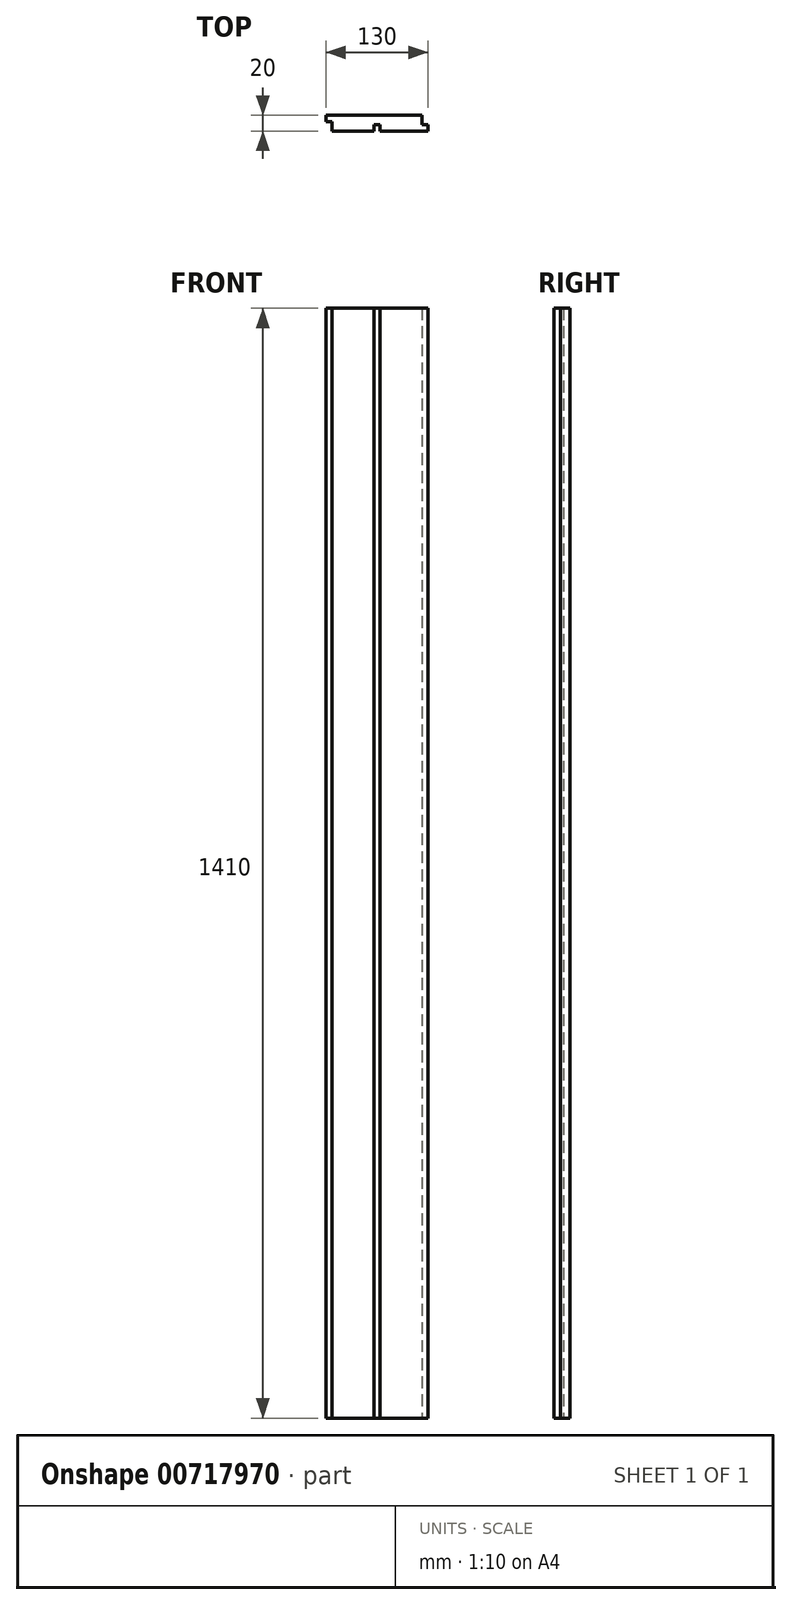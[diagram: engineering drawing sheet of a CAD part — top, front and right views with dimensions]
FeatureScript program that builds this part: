
annotation { "Feature Type Name" : "Feature", "Feature Type Description" : "" }
export const myFeature = defineFeature(function(context is Context, id is Id, definition is map)
    precondition{}
    {
        {
            var Q0;
            Q0=qCreatedBy(makeId("Front.planeOp"),FACE);
            var sketch = newSketch(context, id + "F0", { "sketchPlane" : qUnion([Q0])});
            skLineSegment(sketch, "E0.bottom", {"start": v(-374.72, 1144.48) * mm, "end": v(-244.72, 1144.48) * mm});
            skLineSegment(sketch, "E0.top", {"start": v(-374.72, -265.52) * mm, "end": v(-244.72, -265.52) * mm});
            skLineSegment(sketch, "E0.left", {"start": v(-374.72, 1144.48) * mm, "end": v(-374.72, -265.52) * mm});
            skLineSegment(sketch, "E0.right", {"start": v(-244.72, 1144.48) * mm, "end": v(-244.72, -265.52) * mm});
            skSolve(sketch);
        }
        {
            var Q0;
            Q0=makeQuery(id+"F0.imprint","IMPRINT",FACE,{"disambiguationData":[TD([[makeQuery(id+"F0.imprint","IMPRINT",EDGE,{"derivedFrom":sQuery(id+"F0.wireOp",EDGE,"E0.bottom")}),-1.0]])]});
            extrude(context, id + "F1", {"entities" : qUnion([Q0]), "oppositeDirection" : true, "depth" : 20 * mm, "offsetDistance" : 25.4 * mm});
        }
        {
            var Q0;
            Q0=makeQuery(id+"F1.opExtrude","CAP_FACE",FACE,{"disambiguationData":[OSD([sQuery(id+"F0.wireOp",EDGE,"E0.bottom"),sQuery(id+"F0.wireOp",EDGE,"E0.top"),sQuery(id+"F0.wireOp",EDGE,"E0.left"),sQuery(id+"F0.wireOp",EDGE,"E0.right")])],"isStart":true});
            var sketch = newSketch(context, id + "F2", { "sketchPlane" : qUnion([Q0])});
            skLineSegment(sketch, "E1.bottom", {"start": v(-313.72, 1144.48) * mm, "end": v(-305.72, 1144.48) * mm});
            skLineSegment(sketch, "E1.top", {"start": v(-313.72, -315.52) * mm, "end": v(-305.72, -315.52) * mm});
            skLineSegment(sketch, "E1.left", {"start": v(-313.72, 1144.48) * mm, "end": v(-313.72, -315.52) * mm});
            skLineSegment(sketch, "E1.right", {"start": v(-305.72, 1144.48) * mm, "end": v(-305.72, -315.52) * mm});
            skSolve(sketch);
        }
        {
            var Q0;
            Q0=makeQuery(id+"F2.imprint","IMPRINT",FACE,{"disambiguationData":[TD([[makeQuery(id+"F2.imprint","IMPRINT",EDGE,{"derivedFrom":sQuery(id+"F2.wireOp",EDGE,"E1.bottom")}),-1.0]])]});
            extrude(context, id + "F3", {"entities" : qUnion([Q0]), "operationType" : NewBodyOperationType.REMOVE, "oppositeDirection" : true, "depth" : 8 * mm, "offsetDistance" : 25.4 * mm});
        }
        {
            var Q0;
            {var subQ0=sQuery(id+"F0.wireOp",EDGE,"E0.bottom");var subQ1=sQuery(id+"F0.wireOp",EDGE,"E0.top");var subQ2=sQuery(id+"F0.wireOp",EDGE,"E0.left");Q0=makeQuery(id+"F3.boolean.opBoolean","SPLIT",FACE,{"disambiguationData":[TD([makeQuery(id+"F1.opExtrude","SWEPT_FACE",FACE,{"disambiguationData":[OSD([subQ2])]})])],"derivedFrom":makeQuery(id+"F1.opExtrude","CAP_FACE",FACE,{"disambiguationData":[OSD([subQ0,subQ1,subQ2,sQuery(id+"F0.wireOp",EDGE,"E0.right")])],"isStart":true})});}
            var sketch = newSketch(context, id + "F4", { "sketchPlane" : qUnion([Q0])});
            skLineSegment(sketch, "E2.bottom", {"start": v(-374.72, 1144.48) * mm, "end": v(-366.72, 1144.48) * mm});
            skLineSegment(sketch, "E2.top", {"start": v(-374.72, -315.52) * mm, "end": v(-366.72, -315.52) * mm});
            skLineSegment(sketch, "E2.left", {"start": v(-374.72, 1144.48) * mm, "end": v(-374.72, -315.52) * mm});
            skLineSegment(sketch, "E2.right", {"start": v(-366.72, 1144.48) * mm, "end": v(-366.72, -315.52) * mm});
            skSolve(sketch);
        }
        {
            var Q0;
            Q0=makeQuery(id+"F4.imprint","IMPRINT",FACE,{"disambiguationData":[TD([[makeQuery(id+"F4.imprint","IMPRINT",EDGE,{"derivedFrom":sQuery(id+"F4.wireOp",EDGE,"E2.bottom")}),-1.0]])]});
            extrude(context, id + "F5", {"entities" : qUnion([Q0]), "operationType" : NewBodyOperationType.REMOVE, "oppositeDirection" : true, "depth" : 12 * mm, "offsetDistance" : 25.4 * mm});
        }
        {
            var Q0;
            Q0=makeQuery(id+"F1.opExtrude","CAP_FACE",FACE,{"disambiguationData":[OSD([sQuery(id+"F0.wireOp",EDGE,"E0.bottom"),sQuery(id+"F0.wireOp",EDGE,"E0.top"),sQuery(id+"F0.wireOp",EDGE,"E0.left"),sQuery(id+"F0.wireOp",EDGE,"E0.right")])],"isStart":false});
            var sketch = newSketch(context, id + "F6", { "sketchPlane" : qUnion([Q0])});
            skLineSegment(sketch, "E3.bottom", {"start": v(244.72, 1144.48) * mm, "end": v(252.72, 1144.48) * mm});
            skLineSegment(sketch, "E3.top", {"start": v(244.72, -315.52) * mm, "end": v(252.72, -315.52) * mm});
            skLineSegment(sketch, "E3.left", {"start": v(244.72, 1144.48) * mm, "end": v(244.72, -315.52) * mm});
            skLineSegment(sketch, "E3.right", {"start": v(252.72, 1144.48) * mm, "end": v(252.72, -315.52) * mm});
            skSolve(sketch);
        }
        {
            var Q0;
            Q0=makeQuery(id+"F6.imprint","IMPRINT",FACE,{"disambiguationData":[TD([[makeQuery(id+"F6.imprint","IMPRINT",EDGE,{"derivedFrom":sQuery(id+"F6.wireOp",EDGE,"E3.bottom")}),1.0]])]});
            extrude(context, id + "F7", {"entities" : qUnion([Q0]), "operationType" : NewBodyOperationType.REMOVE, "oppositeDirection" : true, "depth" : 12 * mm, "offsetDistance" : 25.4 * mm});
        }
    });
